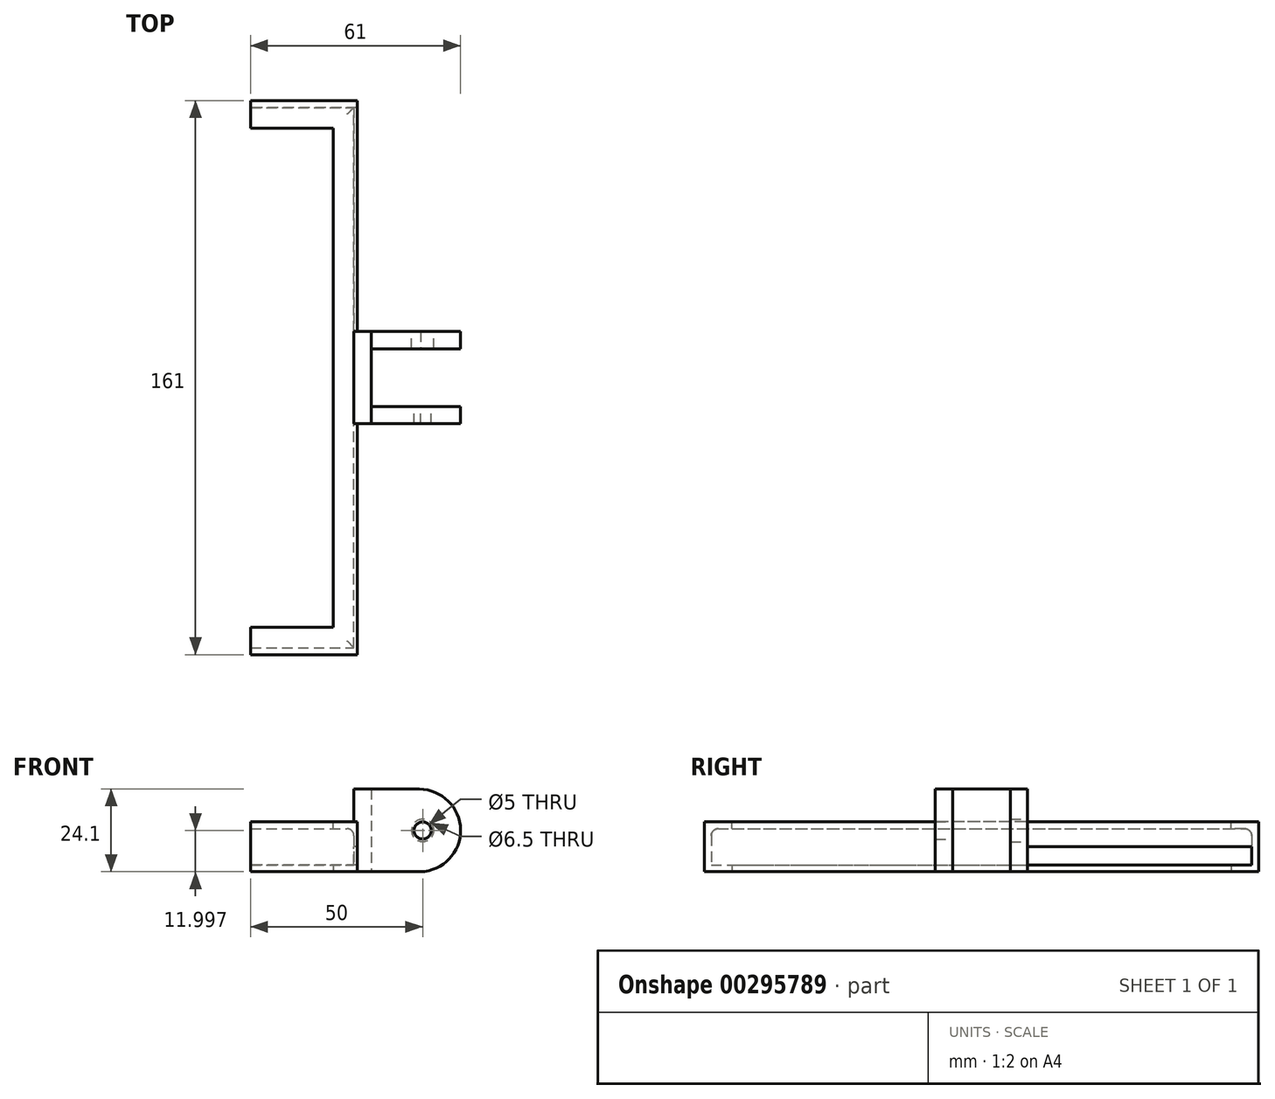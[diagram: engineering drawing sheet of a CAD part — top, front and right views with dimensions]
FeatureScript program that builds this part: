
annotation { "Feature Type Name" : "Feature", "Feature Type Description" : "" }
export const myFeature = defineFeature(function(context is Context, id is Id, definition is map)
    precondition{}
    {
        {
            var Q0;
            Q0=qCreatedBy(makeId("Front.planeOp"),FACE);
            var sketch = newSketch(context, id + "F0", { "sketchPlane" : qUnion([Q0])});
            skLineSegment(sketch, "E0", {"start": v(0, 24) * mm, "end": v(14, 24) * mm});
            skLineSegment(sketch, "E1", {"start": v(0, 24) * mm, "end": v(0, 0) * mm});
            skLineSegment(sketch, "E2", {"start": v(0, 0) * mm, "end": v(14.38, 0) * mm});
            skArc(sketch, "E3", {"start": v(14, 24) * mm, "mid": v(26, 12.19) * mm, "end": v(14.38, 0) * mm});
            skLineSegment(sketch, "E4", {"start": v(14, 12) * mm, "end": v(55.65, 12) * mm, "construction": true});
            skLineSegment(sketch, "E5", {"start": v(26, 12) * mm, "end": v(26, 23.36) * mm, "construction": true});
            skCircle(sketch, "E6", {"center": v(15, 12) * mm, "radius": 2.5 * mm});
            skCircle(sketch, "E7", {"center": v(15, 12) * mm, "radius": 3.3 * mm});
            skLineSegment(sketch, "E8.bottom", {"start": v(0, 0) * mm, "end": v(-5, 0) * mm});
            skLineSegment(sketch, "E8.top", {"start": v(0, 24.1) * mm, "end": v(-5, 24.1) * mm});
            skLineSegment(sketch, "E8.left", {"start": v(0, 0) * mm, "end": v(0, 24.1) * mm});
            skLineSegment(sketch, "E8.right", {"start": v(-5, 0) * mm, "end": v(-5, 24.1) * mm});
            skSolve(sketch);
        }
        {
            var Q0;
            Q0=makeQuery(id+"F0.imprint","IMPRINT",FACE,{"disambiguationData":[TD([[makeQuery(id+"F0.imprint","IMPRINT",EDGE,{"derivedFrom":sQuery(id+"F0.wireOp",EDGE,"E0")}),-1.0]])]});
            var Q1;
            Q1=makeQuery(id+"F0.imprint","IMPRINT",FACE,{"disambiguationData":[TD([[makeQuery(id+"F0.imprint","IMPRINT",EDGE,{"derivedFrom":sQuery(id+"F0.wireOp",EDGE,"E6")}),-1.0]])]});
            extrude(context, id + "F1", {"entities" : qUnion([Q0, Q1]), "depth" : 5 * mm});
        }
        {
            var Q0;
            {var subQ3=sQuery(id+"F0.wireOp",EDGE,"E8.bottom");Q0=makeQuery(id+"F0.imprint","IMPRINT",FACE,{"disambiguationData":[TD([[makeQuery(id+"F0.imprint","IMPRINT",EDGE,{"derivedFrom":subQ3}),-1.0]])]});}
            extrude(context, id + "F2", {"entities" : qUnion([Q0]), "operationType" : NewBodyOperationType.ADD, "depth" : 5 * mm, "hasSecondDirection" : true, "secondDirectionOppositeDirection" : true, "secondDirectionDepth" : 21.8 * mm});
        }
        {
            var Q0;
            {var subQ1=sQuery(id+"F0.wireOp",EDGE,"E0");Q0=makeQuery(id+"F0.imprint","IMPRINT",FACE,{"disambiguationData":[TD([[makeQuery(id+"F0.imprint","IMPRINT",EDGE,{"derivedFrom":subQ1}),-1.0]])]});}
            cPlane(context, id + "F3", {"entities" : qUnion([Q0]), "cplaneType" : CPlaneType.OFFSET, "offset" : 8.4 * mm, "oppositeDirection" : true, "width" : 150 * mm, "height" : 150 * mm});
        }
        {
            var Q0;
            Q0=makeQuery(id+"F1.opExtrude","SWEPT_BODY",BODY,{"disambiguationData":[OSD([sQuery(id+"F0.wireOp",EDGE,"E0"),sQuery(id+"F0.wireOp",EDGE,"E2"),sQuery(id+"F0.wireOp",EDGE,"E3"),sQuery(id+"F0.wireOp",EDGE,"E6"),sQuery(id+"F0.wireOp",EDGE,"E8.left")])]});
            var Q1;
            Q1=qCreatedBy(id+"F3.planeOp",FACE);
            mirror(context, id + "F4", {"operationType" : NewBodyOperationType.ADD, "entities" : qUnion([Q0]), "mirrorPlane" : qUnion([Q1])});
        }
        {
            var Q0;
            {var subQ0=sQuery(id+"F0.wireOp",EDGE,"E8.right");var subQ1=sQuery(id+"F0.wireOp",EDGE,"E8.left");var subQ2=sQuery(id+"F0.wireOp",EDGE,"E8.top");var subQ3=sQuery(id+"F0.wireOp",EDGE,"E8.bottom");Q0=makeQuery(id+"F4.boolean.opBoolean","MERGE",FACE,{"derivedFrom":[makeQuery(id+"F2.opExtrude","CAP_FACE",FACE,{"disambiguationData":[OSD([subQ3,subQ2,subQ1,subQ0])],"isStart":true}),makeQuery(id+"F4.opPattern","COPY",FACE,{"derivedFrom":makeQuery(id+"F2.boolean.opBoolean","MERGE",FACE,{"derivedFrom":[makeQuery(id+"F1.opExtrude","CAP_FACE",FACE,{"disambiguationData":[OSD([sQuery(id+"F0.wireOp",EDGE,"E0"),sQuery(id+"F0.wireOp",EDGE,"E2"),sQuery(id+"F0.wireOp",EDGE,"E3"),sQuery(id+"F0.wireOp",EDGE,"E6"),subQ1])],"isStart":false}),makeQuery(id+"F2.opExtrude","CAP_FACE",FACE,{"disambiguationData":[OSD([subQ3,subQ2,subQ1,subQ0])],"isStart":false})]}),"instanceName":"1"})]});}
            var sketch = newSketch(context, id + "F5", { "sketchPlane" : qUnion([Q0])});
            skCircle(sketch, "E9", {"center": v(-15, 12) * mm, "radius": 3.25 * mm});
            skSolve(sketch);
        }
        {
            var Q0;
            Q0=makeQuery(id+"F5.imprint","IMPRINT",FACE,{"disambiguationData":[TD([[makeQuery(id+"F5.imprint","IMPRINT",EDGE,{"derivedFrom":sQuery(id+"F5.wireOp",EDGE,"E9")}),1.0]])]});
            extrude(context, id + "F6", {"entities" : qUnion([Q0]), "operationType" : NewBodyOperationType.REMOVE, "oppositeDirection" : true, "depth" : 6 * mm});
        }
        {
            var Q0;
            Q0=makeQuery(id+"F2.opExtrude","SWEPT_FACE",FACE,{"disambiguationData":[OSD([sQuery(id+"F0.wireOp",EDGE,"E8.right")])]});
            var sketch = newSketch(context, id + "F7", { "sketchPlane" : qUnion([Q0])});
            skLineSegment(sketch, "E10", {"start": v(-51.17, 12.05) * mm, "end": v(7.57, 12.05) * mm, "construction": true});
            skLineSegment(sketch, "E11", {"start": v(-8.4, 24.1) * mm, "end": v(-8.4, -10.67) * mm, "construction": true});
            skPoint(sketch, "E11.endSnap0", {"position": v(-8.4, 0) * mm});
            skLineSegment(sketch, "E12.bottom", {"start": v(-8.4, 0) * mm, "end": v(-86.9, 0) * mm});
            skLineSegment(sketch, "E12.top", {"start": v(-8.4, 2) * mm, "end": v(-86.9, 2) * mm});
            skLineSegment(sketch, "E12.left", {"start": v(-8.4, 0) * mm, "end": v(-8.4, 2) * mm});
            skLineSegment(sketch, "E12.right", {"start": v(-86.9, 0) * mm, "end": v(-86.9, 2) * mm});
            skLineSegment(sketch, "E13.left", {"start": v(-86.9, 2) * mm, "end": v(-86.9, 1) * mm});
            skLineSegment(sketch, "E14", {"start": v(-96.9, 7.25) * mm, "end": v(13.3, 7.25) * mm, "construction": true});
            skLineSegment(sketch, "E15.bottom", {"start": v(-86.9, 2) * mm, "end": v(-8.4, 2) * mm});
            skLineSegment(sketch, "E15.top", {"start": v(-86.9, 7.25) * mm, "end": v(-8.4, 7.25) * mm});
            skLineSegment(sketch, "E15.left", {"start": v(-86.9, 2) * mm, "end": v(-86.9, 7.25) * mm});
            skLineSegment(sketch, "E15.right", {"start": v(-8.4, 2) * mm, "end": v(-8.4, 7.25) * mm});
            skLineSegment(sketch, "E16.bottom", {"start": v(-86.9, 0) * mm, "end": v(-88.9, 0) * mm});
            skLineSegment(sketch, "E16.top", {"start": v(-86.9, 7.25) * mm, "end": v(-88.9, 7.25) * mm});
            skLineSegment(sketch, "E16.left", {"start": v(-86.9, 0) * mm, "end": v(-86.9, 7.25) * mm});
            skLineSegment(sketch, "E16.right", {"start": v(-88.9, 0) * mm, "end": v(-88.9, 7.25) * mm});
            skLineSegment(sketch, "E17.MirrorCS", {"start": v(-86.9, 12.5) * mm, "end": v(-8.4, 12.5) * mm});
            skLineSegment(sketch, "E18.MirrorCS", {"start": v(-8.4, 14.5) * mm, "end": v(-86.9, 14.5) * mm});
            skLineSegment(sketch, "E19.MirrorCS", {"start": v(-88.9, 14.5) * mm, "end": v(-88.9, 7.25) * mm});
            skLineSegment(sketch, "E20.MirrorCS", {"start": v(-86.9, 12.5) * mm, "end": v(-86.9, 7.25) * mm});
            skLineSegment(sketch, "E21.MirrorCS", {"start": v(-86.9, 14.5) * mm, "end": v(-88.9, 14.5) * mm});
            skLineSegment(sketch, "E22.MirrorCS", {"start": v(70.1, 12.5) * mm, "end": v(-8.4, 12.5) * mm});
            skLineSegment(sketch, "E23.MirrorCS", {"start": v(-8.4, 14.5) * mm, "end": v(70.1, 14.5) * mm});
            skLineSegment(sketch, "E24.MirrorCS", {"start": v(70.1, 2) * mm, "end": v(-8.4, 2) * mm});
            skLineSegment(sketch, "E25.MirrorCS", {"start": v(-8.4, 0) * mm, "end": v(70.1, 0) * mm});
            skLineSegment(sketch, "E26.MirrorCS", {"start": v(70.1, 12.5) * mm, "end": v(70.1, 7.25) * mm});
            skLineSegment(sketch, "E27.MirrorCS", {"start": v(72.1, 14.5) * mm, "end": v(72.1, 7.25) * mm});
            skLineSegment(sketch, "E28.MirrorCS", {"start": v(72.1, 0) * mm, "end": v(72.1, 7.25) * mm});
            skLineSegment(sketch, "E29.MirrorCS", {"start": v(70.1, 2) * mm, "end": v(70.1, 7.25) * mm});
            skLineSegment(sketch, "E30.MirrorCS", {"start": v(70.1, 14.5) * mm, "end": v(72.1, 14.5) * mm});
            skLineSegment(sketch, "E31.MirrorCS", {"start": v(70.1, 0) * mm, "end": v(72.1, 0) * mm});
            skLineSegment(sketch, "E32", {"start": v(-86.9, 12.5) * mm, "end": v(-86.9, 14.5) * mm});
            skLineSegment(sketch, "E33", {"start": v(-80.9, 14.5) * mm, "end": v(-80.9, 12.5) * mm});
            skLineSegment(sketch, "E34.MirrorCS", {"start": v(-80.9, 0) * mm, "end": v(-80.9, 2) * mm});
            skLineSegment(sketch, "E35.MirrorCS", {"start": v(64.1, 14.5) * mm, "end": v(64.1, 12.5) * mm});
            skLineSegment(sketch, "E36.MirrorCS", {"start": v(64.1, 0) * mm, "end": v(64.1, 2) * mm});
            skLineSegment(sketch, "E37.MirrorCS", {"start": v(70.1, 2) * mm, "end": v(70.1, 1) * mm});
            skLineSegment(sketch, "E38.MirrorCS", {"start": v(70.1, 12.5) * mm, "end": v(70.1, 14.5) * mm});
            skSolve(sketch);
        }
        {
            var Q0;
            {var subQ8=sQuery(id+"F7.wireOp",EDGE,"E26.MirrorCS");Q0=makeQuery(id+"F7.imprint","IMPRINT",FACE,{"disambiguationData":[TD([[makeQuery(id+"F7.imprint","IMPRINT",EDGE,{"derivedFrom":subQ8}),-1.0]])]});}
            var Q1;
            {var subQ0=sQuery(id+"F7.wireOp",EDGE,"E35.MirrorCS");Q1=makeQuery(id+"F7.imprint","IMPRINT",FACE,{"disambiguationData":[TD([[makeQuery(id+"F7.imprint","IMPRINT",EDGE,{"derivedFrom":subQ0}),-1.0]])]});}
            var Q2;
            {var subQ0=sQuery(id+"F7.wireOp",EDGE,"E36.MirrorCS");Q2=makeQuery(id+"F7.imprint","IMPRINT",FACE,{"disambiguationData":[TD([[makeQuery(id+"F7.imprint","IMPRINT",EDGE,{"derivedFrom":subQ0}),1.0]])]});}
            var Q3;
            {var subQ2=sQuery(id+"F7.wireOp",EDGE,"E35.MirrorCS");Q3=makeQuery(id+"F7.imprint","IMPRINT",FACE,{"disambiguationData":[TD([[makeQuery(id+"F7.imprint","IMPRINT",EDGE,{"derivedFrom":subQ2}),1.0]])]});}
            var Q4;
            Q4=makeQuery(id+"F7.imprint","IMPRINT",FACE,{"disambiguationData":[TD([[makeQuery(id+"F7.imprint","IMPRINT",EDGE,{"derivedFrom":sQuery(id+"F7.wireOp",EDGE,"E26.MirrorCS")}),1.0]])]});
            var Q5;
            {var subQ2=sQuery(id+"F7.wireOp",EDGE,"E36.MirrorCS");Q5=makeQuery(id+"F7.imprint","IMPRINT",FACE,{"disambiguationData":[TD([[makeQuery(id+"F7.imprint","IMPRINT",EDGE,{"derivedFrom":subQ2}),-1.0]])]});}
            var Q6;
            {var subQ4=sQuery(id+"F7.wireOp",EDGE,"E20.MirrorCS");Q6=makeQuery(id+"F7.imprint","IMPRINT",FACE,{"disambiguationData":[TD([[makeQuery(id+"F7.imprint","IMPRINT",EDGE,{"derivedFrom":subQ4}),1.0]])]});}
            var Q7;
            {var subQ3=sQuery(id+"F7.wireOp",EDGE,"E34.MirrorCS");Q7=makeQuery(id+"F7.imprint","IMPRINT",FACE,{"disambiguationData":[TD([[makeQuery(id+"F7.imprint","IMPRINT",EDGE,{"derivedFrom":subQ3}),-1.0]])]});}
            var Q8;
            {var subQ0=sQuery(id+"F7.wireOp",EDGE,"E16.left");var subQ1=sQuery(id+"F7.wireOp",EDGE,"E15.bottom");var subQ2=makeQuery(id+"F7.imprint","INTERSECT",VERTEX,{"derivedFrom":[subQ1,subQ0]});Q8=makeQuery(id+"F7.imprint","IMPRINT",FACE,{"disambiguationData":[TD([[makeQuery(id+"F7.imprint","IMPRINT",EDGE,{"disambiguationData":[TD([[subQ2,-1.0]])],"derivedFrom":subQ1}),1.0]])]});}
            var Q9;
            {var subQ3=sQuery(id+"F7.wireOp",EDGE,"E16.bottom");Q9=makeQuery(id+"F7.imprint","IMPRINT",FACE,{"disambiguationData":[TD([[makeQuery(id+"F7.imprint","IMPRINT",EDGE,{"derivedFrom":subQ3}),-1.0]])]});}
            var Q10;
            Q10=makeQuery(id+"F7.imprint","IMPRINT",FACE,{"disambiguationData":[TD([[makeQuery(id+"F7.imprint","IMPRINT",EDGE,{"derivedFrom":sQuery(id+"F7.wireOp",EDGE,"E16.top")}),-1.0]])]});
            var Q11;
            {var subQ0=sQuery(id+"F7.wireOp",EDGE,"E32");Q11=makeQuery(id+"F7.imprint","IMPRINT",FACE,{"disambiguationData":[TD([[makeQuery(id+"F7.imprint","IMPRINT",EDGE,{"derivedFrom":subQ0}),-1.0]])]});}
            var Q12;
            {var subQ0=sQuery(id+"F7.wireOp",EDGE,"E33");Q12=makeQuery(id+"F7.imprint","IMPRINT",FACE,{"disambiguationData":[TD([[makeQuery(id+"F7.imprint","IMPRINT",EDGE,{"derivedFrom":subQ0}),1.0]])]});}
            var Q13;
            {var subQ3=sQuery(id+"F7.wireOp",EDGE,"E34.MirrorCS");Q13=makeQuery(id+"F7.imprint","IMPRINT",FACE,{"disambiguationData":[TD([[makeQuery(id+"F7.imprint","IMPRINT",EDGE,{"derivedFrom":subQ3}),1.0]])]});}
            extrude(context, id + "F8", {"entities" : qUnion([Q0, Q1, Q2, Q3, Q4, Q5, Q6, Q7, Q8, Q9, Q10, Q11, Q12, Q13]), "operationType" : NewBodyOperationType.ADD, "oppositeDirection" : true, "depth" : 1 * mm});
        }
        {
            var Q0;
            {var subQ0=sQuery(id+"F7.wireOp",EDGE,"E35.MirrorCS");Q0=makeQuery(id+"F7.imprint","IMPRINT",FACE,{"disambiguationData":[TD([[makeQuery(id+"F7.imprint","IMPRINT",EDGE,{"derivedFrom":subQ0}),-1.0]])]});}
            var Q1;
            {var subQ2=sQuery(id+"F7.wireOp",EDGE,"E35.MirrorCS");Q1=makeQuery(id+"F7.imprint","IMPRINT",FACE,{"disambiguationData":[TD([[makeQuery(id+"F7.imprint","IMPRINT",EDGE,{"derivedFrom":subQ2}),1.0]])]});}
            var Q2;
            Q2=makeQuery(id+"F7.imprint","IMPRINT",FACE,{"disambiguationData":[TD([[makeQuery(id+"F7.imprint","IMPRINT",EDGE,{"derivedFrom":sQuery(id+"F7.wireOp",EDGE,"E26.MirrorCS")}),1.0]])]});
            var Q3;
            {var subQ2=sQuery(id+"F7.wireOp",EDGE,"E36.MirrorCS");Q3=makeQuery(id+"F7.imprint","IMPRINT",FACE,{"disambiguationData":[TD([[makeQuery(id+"F7.imprint","IMPRINT",EDGE,{"derivedFrom":subQ2}),-1.0]])]});}
            var Q4;
            {var subQ0=sQuery(id+"F7.wireOp",EDGE,"E36.MirrorCS");Q4=makeQuery(id+"F7.imprint","IMPRINT",FACE,{"disambiguationData":[TD([[makeQuery(id+"F7.imprint","IMPRINT",EDGE,{"derivedFrom":subQ0}),1.0]])]});}
            var Q5;
            {var subQ3=sQuery(id+"F7.wireOp",EDGE,"E12.left");Q5=makeQuery(id+"F7.imprint","IMPRINT",FACE,{"disambiguationData":[TD([[makeQuery(id+"F7.imprint","IMPRINT",EDGE,{"derivedFrom":subQ3}),1.0]])]});}
            var Q6;
            {var subQ0=sQuery(id+"F7.wireOp",EDGE,"E12.left");Q6=makeQuery(id+"F7.imprint","IMPRINT",FACE,{"disambiguationData":[TD([[makeQuery(id+"F7.imprint","IMPRINT",EDGE,{"derivedFrom":subQ0}),-1.0]])]});}
            var Q7;
            {var subQ0=sQuery(id+"F7.wireOp",EDGE,"E22.MirrorCS");var subQ1=sQuery(id+"F7.wireOp",EDGE,"E17.MirrorCS");var subQ2=makeQuery(id+"F7.imprint","INTERSECT",VERTEX,{"derivedFrom":[subQ1,subQ0]});Q7=makeQuery(id+"F7.imprint","IMPRINT",FACE,{"disambiguationData":[TD([[makeQuery(id+"F7.imprint","IMPRINT",EDGE,{"disambiguationData":[TD([[subQ2,1.0]])],"derivedFrom":subQ1}),1.0]])]});}
            var Q8;
            {var subQ0=sQuery(id+"F7.wireOp",EDGE,"E33");Q8=makeQuery(id+"F7.imprint","IMPRINT",FACE,{"disambiguationData":[TD([[makeQuery(id+"F7.imprint","IMPRINT",EDGE,{"derivedFrom":subQ0}),1.0]])]});}
            var Q9;
            {var subQ3=sQuery(id+"F7.wireOp",EDGE,"E34.MirrorCS");Q9=makeQuery(id+"F7.imprint","IMPRINT",FACE,{"disambiguationData":[TD([[makeQuery(id+"F7.imprint","IMPRINT",EDGE,{"derivedFrom":subQ3}),-1.0]])]});}
            var Q10;
            {var subQ0=sQuery(id+"F7.wireOp",EDGE,"E32");Q10=makeQuery(id+"F7.imprint","IMPRINT",FACE,{"disambiguationData":[TD([[makeQuery(id+"F7.imprint","IMPRINT",EDGE,{"derivedFrom":subQ0}),-1.0]])]});}
            var Q11;
            Q11=makeQuery(id+"F7.imprint","IMPRINT",FACE,{"disambiguationData":[TD([[makeQuery(id+"F7.imprint","IMPRINT",EDGE,{"derivedFrom":sQuery(id+"F7.wireOp",EDGE,"E16.top")}),-1.0]])]});
            var Q12;
            {var subQ3=sQuery(id+"F7.wireOp",EDGE,"E16.bottom");Q12=makeQuery(id+"F7.imprint","IMPRINT",FACE,{"disambiguationData":[TD([[makeQuery(id+"F7.imprint","IMPRINT",EDGE,{"derivedFrom":subQ3}),-1.0]])]});}
            var Q13;
            {var subQ3=sQuery(id+"F7.wireOp",EDGE,"E34.MirrorCS");Q13=makeQuery(id+"F7.imprint","IMPRINT",FACE,{"disambiguationData":[TD([[makeQuery(id+"F7.imprint","IMPRINT",EDGE,{"derivedFrom":subQ3}),1.0]])]});}
            extrude(context, id + "F9", {"entities" : qUnion([Q0, Q1, Q2, Q3, Q4, Q5, Q6, Q7, Q8, Q9, Q10, Q11, Q12, Q13]), "operationType" : NewBodyOperationType.ADD, "depth" : 6 * mm});
        }
        {
            var Q0;
            {var subQ0=sQuery(id+"F7.wireOp",EDGE,"E32");Q0=makeQuery(id+"F7.imprint","IMPRINT",FACE,{"disambiguationData":[TD([[makeQuery(id+"F7.imprint","IMPRINT",EDGE,{"derivedFrom":subQ0}),-1.0]])]});}
            var Q1;
            Q1=makeQuery(id+"F7.imprint","IMPRINT",FACE,{"disambiguationData":[TD([[makeQuery(id+"F7.imprint","IMPRINT",EDGE,{"derivedFrom":sQuery(id+"F7.wireOp",EDGE,"E16.top")}),-1.0]])]});
            var Q2;
            {var subQ3=sQuery(id+"F7.wireOp",EDGE,"E16.bottom");Q2=makeQuery(id+"F7.imprint","IMPRINT",FACE,{"disambiguationData":[TD([[makeQuery(id+"F7.imprint","IMPRINT",EDGE,{"derivedFrom":subQ3}),-1.0]])]});}
            var Q3;
            {var subQ3=sQuery(id+"F7.wireOp",EDGE,"E34.MirrorCS");Q3=makeQuery(id+"F7.imprint","IMPRINT",FACE,{"disambiguationData":[TD([[makeQuery(id+"F7.imprint","IMPRINT",EDGE,{"derivedFrom":subQ3}),1.0]])]});}
            var Q4;
            Q4=makeQuery(id+"F7.imprint","IMPRINT",FACE,{"disambiguationData":[TD([[makeQuery(id+"F7.imprint","IMPRINT",EDGE,{"derivedFrom":sQuery(id+"F7.wireOp",EDGE,"E26.MirrorCS")}),1.0]])]});
            var Q5;
            {var subQ2=sQuery(id+"F7.wireOp",EDGE,"E36.MirrorCS");Q5=makeQuery(id+"F7.imprint","IMPRINT",FACE,{"disambiguationData":[TD([[makeQuery(id+"F7.imprint","IMPRINT",EDGE,{"derivedFrom":subQ2}),-1.0]])]});}
            var Q6;
            {var subQ2=sQuery(id+"F7.wireOp",EDGE,"E35.MirrorCS");Q6=makeQuery(id+"F7.imprint","IMPRINT",FACE,{"disambiguationData":[TD([[makeQuery(id+"F7.imprint","IMPRINT",EDGE,{"derivedFrom":subQ2}),1.0]])]});}
            extrude(context, id + "F10", {"entities" : qUnion([Q0, Q1, Q2, Q3, Q4, Q5, Q6]), "operationType" : NewBodyOperationType.ADD, "depth" : 30 * mm});
        }
        {
            var Q0;
            {var subQ0=sQuery(id+"F7.wireOp",EDGE,"E38.MirrorCS");var subQ1=sQuery(id+"F7.wireOp",EDGE,"E26.MirrorCS");var subQ2=sQuery(id+"F7.wireOp",EDGE,"E22.MirrorCS");Q0=makeQuery(id+"F10.boolean.opBoolean","MERGE",EDGE,{"derivedFrom":[makeQuery(id+"F9.opExtrude","SWEPT_EDGE",EDGE,{"disambiguationData":[OSD([subQ2,subQ1,subQ0])]}),makeQuery(id+"F10.opExtrude","SWEPT_EDGE",EDGE,{"disambiguationData":[OSD([subQ2,subQ1,subQ0])]})]});}
            var Q1;
            Q1=makeQuery(id+"F9.opExtrude","CAP_EDGE",EDGE,{"disambiguationData":[OSD([sQuery(id+"F7.wireOp",EDGE,"E17.MirrorCS"),sQuery(id+"F7.wireOp",EDGE,"E22.MirrorCS")])],"isStart":true});
            var Q2;
            {var subQ0=sQuery(id+"F7.wireOp",EDGE,"E32");var subQ1=sQuery(id+"F7.wireOp",EDGE,"E20.MirrorCS");var subQ2=sQuery(id+"F7.wireOp",EDGE,"E17.MirrorCS");Q2=makeQuery(id+"F10.boolean.opBoolean","MERGE",EDGE,{"derivedFrom":[makeQuery(id+"F9.opExtrude","SWEPT_EDGE",EDGE,{"disambiguationData":[OSD([subQ2,subQ1,subQ0])]}),makeQuery(id+"F10.opExtrude","SWEPT_EDGE",EDGE,{"disambiguationData":[OSD([subQ2,subQ1,subQ0])]})]});}
            fillet(context, id + "F11", {"entities" : qUnion([Q0, Q1, Q2]), "radius" : 2 * mm, "tangentPropagation" : true, "allowEdgeOverflow" : false});
        }
    });
